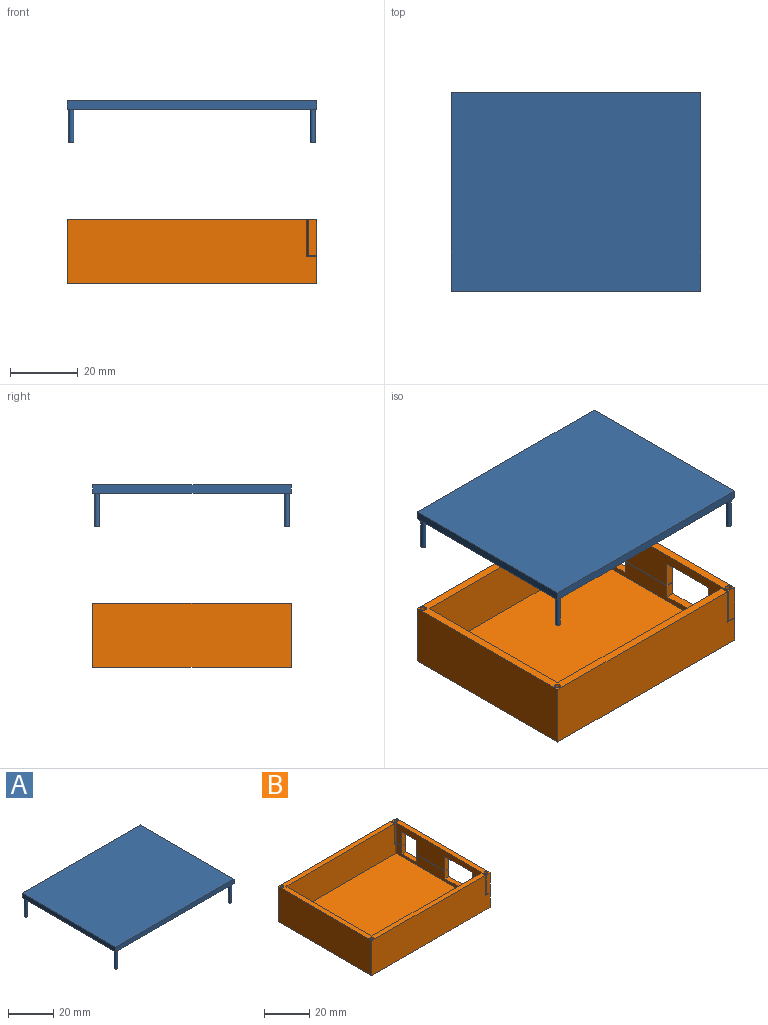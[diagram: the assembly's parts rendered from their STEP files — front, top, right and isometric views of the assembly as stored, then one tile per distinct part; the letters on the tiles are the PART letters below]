
ASSEMBLY  parts=2 mates=1
PART A: 14 faces, bbox 74x58.8x12.5 mm
  f0: plane 58.8x2.5mm, normal (1,0,0), area 147mm2, adj f1,f3,f4,f5
  f1: plane 74x2.5mm, normal (0,1,0), area 185mm2, adj f0,f2,f4,f5
  f2: plane 58.8x2.5mm, normal (-1,0,0), area 147mm2, adj f1,f3,f4,f5
  f3: plane 74x2.5mm, normal (0,-1,0), area 185mm2, adj f0,f2,f4,f5
  f4: plane 74x58.8mm, normal (0,0,1), area 4351.2mm2, adj f0,f1,f2,f3
  f5: plane 74x58.8mm, normal (0,0,-1), area 4344.1mm2, adj f0,f1,f2,f3,f6,f8,f10,f12
  f6: cylinder r=0.75mm len=10mm, axis (0,0,1), area 47.1mm2, adj f5,f7
  f7: plane 1.5x1.5mm, normal (0,0,-1), area 1.8mm2, adj f6
  f8: cylinder r=0.75mm len=10mm, axis (0,0,1), area 47.1mm2, adj f5,f9
  f9: plane 1.5x1.5mm, normal (0,0,-1), area 1.8mm2, adj f8
  f10: cylinder r=0.75mm len=10mm, axis (0,0,1), area 47.1mm2, adj f5,f11
  f11: plane 1.5x1.5mm, normal (0,0,-1), area 1.8mm2, adj f10
  f12: cylinder r=0.75mm len=1.5mm, axis (0,0,1), area 3.8mm2, adj f5,f13
  f13: plane 1.5x1.5mm, normal (0,0,-1), area 1.8mm2, adj f12
PART B: 62 faces, bbox 74x58.8x19 mm
  f0: plane 10.8x2.5mm, normal (0,-1,0), area 27mm2, adj f5,f12,f18,f52
  f1: plane 7.8x2.5mm, normal (0,-1,0), area 19.5mm2, adj f5,f12,f32,f44
  f2: plane 7.8x2.5mm, normal (0,1,0), area 19.5mm2, adj f5,f12,f32,f54
  f3: plane 7.8x2.5mm, normal (0,-1,0), area 19.5mm2, adj f5,f12,f33,f54
  f4: plane 7.8x2.5mm, normal (0,1,0), area 19.5mm2, adj f5,f12,f33,f52
  f5: plane 56.3x10.8mm, normal (-1,0,0), area 399mm2, adj f0,f1,f2,f3,f4,f7,f18,f32
  f6: plane 53.8x5.5mm, normal (-1,0,0), area 188.7mm2, adj f13,f14,f15,f16,f20,f28,f30,f31
  f7: plane 10.8x0mm, normal (0,-1,0), area 0mm2, adj f5,f18,f44,f48
  f8: plane 74x19mm, normal (0,1,0), area 1365.7mm2, adj f21,f24,f26,f27,f48,f49,f51,f55
  f9: plane 74x19mm, normal (0,-1,0), area 1373mm2, adj f21,f24,f26,f27,f46,f47
  f10: cylinder r=0.68mm len=1.13mm, axis (0,0,1), area 0.5mm2, adj f17,f23,f42,f44
  f11: cylinder r=0.68mm len=1.13mm, axis (0,0,1), area 0.5mm2, adj f17,f23,f43,f44
  f12: plane 58.8x10.8mm, normal (1,0,0), area 426mm2, adj f0,f1,f2,f3,f4,f18,f25,f32
  f13: plane 4x2.5mm, normal (0,-1,0), area 10mm2, adj f6,f24,f31,f55
  f14: plane 4x2.5mm, normal (0,1,0), area 10mm2, adj f6,f24,f31,f53
  f15: plane 4x2.5mm, normal (0,-1,0), area 10mm2, adj f6,f24,f34,f53
  f16: plane 4x2.5mm, normal (0,1,0), area 10mm2, adj f6,f24,f34,f47
  f17: plane 0.3x0mm, normal (0,-1,0), area 0mm2, adj f10,f11,f23,f44
  f18: plane 58.8x3.01mm, normal (0,0,1), area 143.1mm2, adj f0,f5,f7,f12,f22,f25,f39,f48
  f19: plane 68.24x16.5mm, normal (0,-1,0), area 1126mm2, adj f21,f29,f30,f49
  f20: plane 69x16.5mm, normal (0,1,0), area 1133mm2, adj f6,f21,f29,f30,f46,f47
  f21: plane 71x58.8mm, normal (0,0,1), area 483.5mm2, adj f8,f9,f19,f20,f26,f29,f35,f37
  f22: cylinder r=0.88mm len=10.5mm, axis (0,0,1), area 47.4mm2, adj f18,f23,f41,f42,f43
  f23: plane 1.75x1.59mm, normal (0,0,1), area 0.8mm2, adj f10,f11,f17,f22,f42,f43
  f24: plane 58.8x8mm, normal (1,0,0), area 363.2mm2, adj f8,f9,f13,f14,f15,f16,f27,f31
  f25: plane 10.8x2.48mm, normal (0,1,0), area 26.8mm2, adj f12,f18,f44,f48
  f26: plane 58.8x19mm, normal (-1,0,0), area 1117.2mm2, adj f8,f9,f21,f27
  f27: plane 74x58.8mm, normal (0,0,-1), area 4351.2mm2, adj f8,f9,f24,f26
  f28: plane 5.5x0mm, normal (0,-1,0), area 0mm2, adj f6,f30,f48,f55
  f29: plane 53.8x16.5mm, normal (1,0,0), area 887.7mm2, adj f19,f20,f21,f30
  f30: plane 69x53.8mm, normal (0,0,1), area 3712.2mm2, adj f6,f19,f20,f28,f29,f50
  f31: plane 9.5x2.5mm, normal (0,0,1), area 23.7mm2, adj f6,f13,f14,f24
  f32: plane 9.5x2.5mm, normal (0,0,-1), area 23.7mm2, adj f1,f2,f5,f12
  f33: plane 17.3x2.5mm, normal (0,0,-1), area 43.2mm2, adj f3,f4,f5,f12
  f34: plane 17.3x2.5mm, normal (0,0,1), area 43.2mm2, adj f6,f15,f16,f24
  f35: cylinder r=0.88mm len=10.5mm, axis (0,0,1), area 57.7mm2, adj f21,f36
  f36: plane 1.75x1.75mm, normal (0,0,1), area 2.4mm2, adj f35
  f37: cylinder r=0.88mm len=10.5mm, axis (0,0,1), area 57.7mm2, adj f21,f38
  f38: plane 1.75x1.75mm, normal (0,0,1), area 2.4mm2, adj f37
  f39: cylinder r=0.88mm len=10.5mm, axis (0,0,1), area 57.7mm2, adj f18,f40
  f40: plane 1.75x1.75mm, normal (0,0,1), area 2.4mm2, adj f39
  f41: plane 1.38x1mm, normal (0,0,1), area 0.9mm2, adj f22,f42,f43,f45,f59
  f42: plane 10x0.72mm, normal (1,0,0), area 7.1mm2, adj f10,f22,f23,f41,f44,f45
  f43: plane 10x0.72mm, normal (-1,0,0), area 7.1mm2, adj f11,f22,f23,f41,f44,f45
  f44: plane 6x2.58mm, normal (0,0,-1), area 14.5mm2, adj f1,f5,f7,f10,f11,f12,f17,f25
  f45: cylinder r=0.5mm len=10mm, axis (0,0,-1), area 15.7mm2, adj f41,f42,f43,f44
  f46: plane 11x2.5mm, normal (1,0,0), area 27.5mm2, adj f9,f20,f21,f47
  f47: plane 8.5x3mm, normal (0,0,1), area 22.5mm2, adj f6,f9,f16,f20,f24,f46
  f48: cylinder r=1.77mm len=17mm, axis (0,0,1), area 47.1mm2, adj f7,f8,f18,f25,f28,f44,f50,f51
  f49: cylinder r=2.37mm len=17mm, axis (0,0,1), area 44.8mm2, adj f8,f19,f21,f50,f51
  f50: plane 0.76x0.5mm, normal (0,1,0), area 0.4mm2, adj f30,f48,f49,f51
  f51: plane 2.5x1.13mm, normal (0,0,1), area 1.6mm2, adj f8,f48,f49,f50
  f52: plane 8.5x2.5mm, normal (0,0,-1), area 21.2mm2, adj f0,f4,f5,f12
  f53: plane 17.5x2.5mm, normal (0,0,1), area 43.7mm2, adj f6,f14,f15,f24
  f54: plane 17.5x2.5mm, normal (0,0,-1), area 43.7mm2, adj f2,f3,f5,f12
  f55: plane 6x2.58mm, normal (0,0,1), area 14.9mm2, adj f6,f8,f13,f24,f28,f48,f56,f58
  f56: plane 2.31x0.2mm, normal (1,0,0), area 0.5mm2, adj f44,f48,f55
  f57: plane 0.6x0.6mm, normal (0,0,1), area 0.2mm2, adj f58,f60
  f58: cylinder r=0.3mm len=0.6mm, axis (0,0,1), area 0.1mm2, adj f55,f57
  f59: cylinder r=0.3mm len=10mm, axis (0,0,1), area 18.7mm2, adj f41,f44
  f60: cylinder r=0.2mm len=10.05mm, axis (0,0,-1), area 12.5mm2, adj f57,f61
  f61: plane 0.4x0.4mm, normal (0,0,1), area 0.1mm2, adj f60
PLACE A t=(-8.88,-4.35,12.16)mm
PLACE B t=(-8.89,-4.35,-39.37)mm
MATE slider B.f58 <-> A.f12  axis (0,0,1) through (26.87,23.8,-21.37)mm
